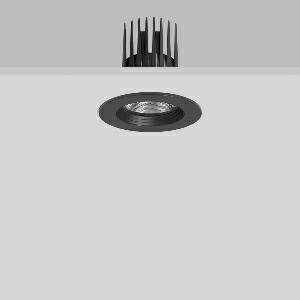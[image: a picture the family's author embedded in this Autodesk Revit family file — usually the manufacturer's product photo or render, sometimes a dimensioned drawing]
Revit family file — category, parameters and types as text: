
# Revit family: heledon_mini_e_901741_003_76_3ae9
name_source: partatom
category: Lighting Fixtures
units: mm (PartAtom-declared; Revit-internal decimal feet)

## family parameters
Cut with Voids When Loaded = No
Host = Face
Light Source = No
Part Type = Normal
Room Calculation Point = No
Round Connector Dimension = Use Diameter
Shared = No

## types (1)
- HELEDON mini E (1 x LED Modul 930, 2450 lm, 3000)
    Apparent Load = 20 VA
    Approval mark = CE
    CIE Flux Codes = 99 100 100 100 100
    Color Rendering = 90
    Color Temperature = 3000
    Default Elevation = 1800 mm
    Description = Series: HELEDON mini
Round recessed downlight. Housing: die-cast aluminium, powder-coated. Black plastic ring and recessed LED to prevent glare from the side. Optical assembly with reflector made of MIRO-Silver with 98% total light reflection for outstanding efficiency - can be changed without tools. Best colour rendering index Ra>90. Suitable for Recessed ceiling mounting. Installation without tools thanks to spring fastening system. Including separate LED converter with connecting cable 600 mm.High quality converter without flickering and stroboscopic effect. Through-wiring box (5 pole) available as accessory. The following accessories can be mounted without use of tools: interchangeable lenses, decorative glasses, honeycomb louvre, clear and frosted diffusers, white interchangeable plastic ring. 
Colour: deep black, matt (RAL 9005)
Diameter: 124 mm
Height: 3 mm
Cut-out diameter: 114 mm
Recess height: 170 mm
Luminaire: recess height: 120 mm
Lamp: LED
Socket: without socket
Colour temperature: 3000K
Colour rendering index (CRI): 92
System power: 20 W
Rated luminous flux: 2450 lm
Luminous efficiency: 123 lm/W
Control gear: Converter, dimmable, DALI
Protection class: II
Type of protection: IP 20
    Height = 0 mm  [stored 0 ft]
    Lamp = 1 x LED Modul 930
    Lamp Light Flux = 2450 lm
    Lamp count = 1
    Length = 124 mm  [stored 0.406824 ft]
    Lifetime = 50000 h
    Luminous efficacy = 123 lm/W
    Manufacturer = RZB
    ModVariant = No
    Model = 901741.003.76
    Mounting Place = Ceiling
    Mounting Type = Recessed
    Number of Poles = 1
    OnlyDefault = Yes
    Power Factor = 1
    Product Name = HELEDON mini E
    Product group = Recessed downlights
    ProductGroupID = 402
    Protection Class = Protection class II
    Protection Degree = IP 20
    RLX_Detail_Level = 1
    RLX_Emergency_Light_Flux = 0 lm
    RLX_Emergency_Type = 0
    RLX_Emergency_Type_DB = No
    RlxData = <blob elided: 127673 chars, md5=2f066c30>
    Socket = socket
    Standby Power = 0 W
    System Light Flux = 2450 lm
    System Power = 20 W
    Type Comments = Product without accessories
    Type Image = 901657.003.jpg
    URL = http://relux.com
    VarID = ---
    Voltage = 230 V
    Voltage Range = 220-240 V
    Weight = 0.00 kg
    Width = 0 mm  [stored 0 ft]

note: [stored X ft] marks values corroborated as IEEE doubles in the binary element streams (Revit-internal decimal feet)

## geometry (parser evidence)
native form markers: Blend x4, Sweep x13
no freeform markers — native parametric forms only
